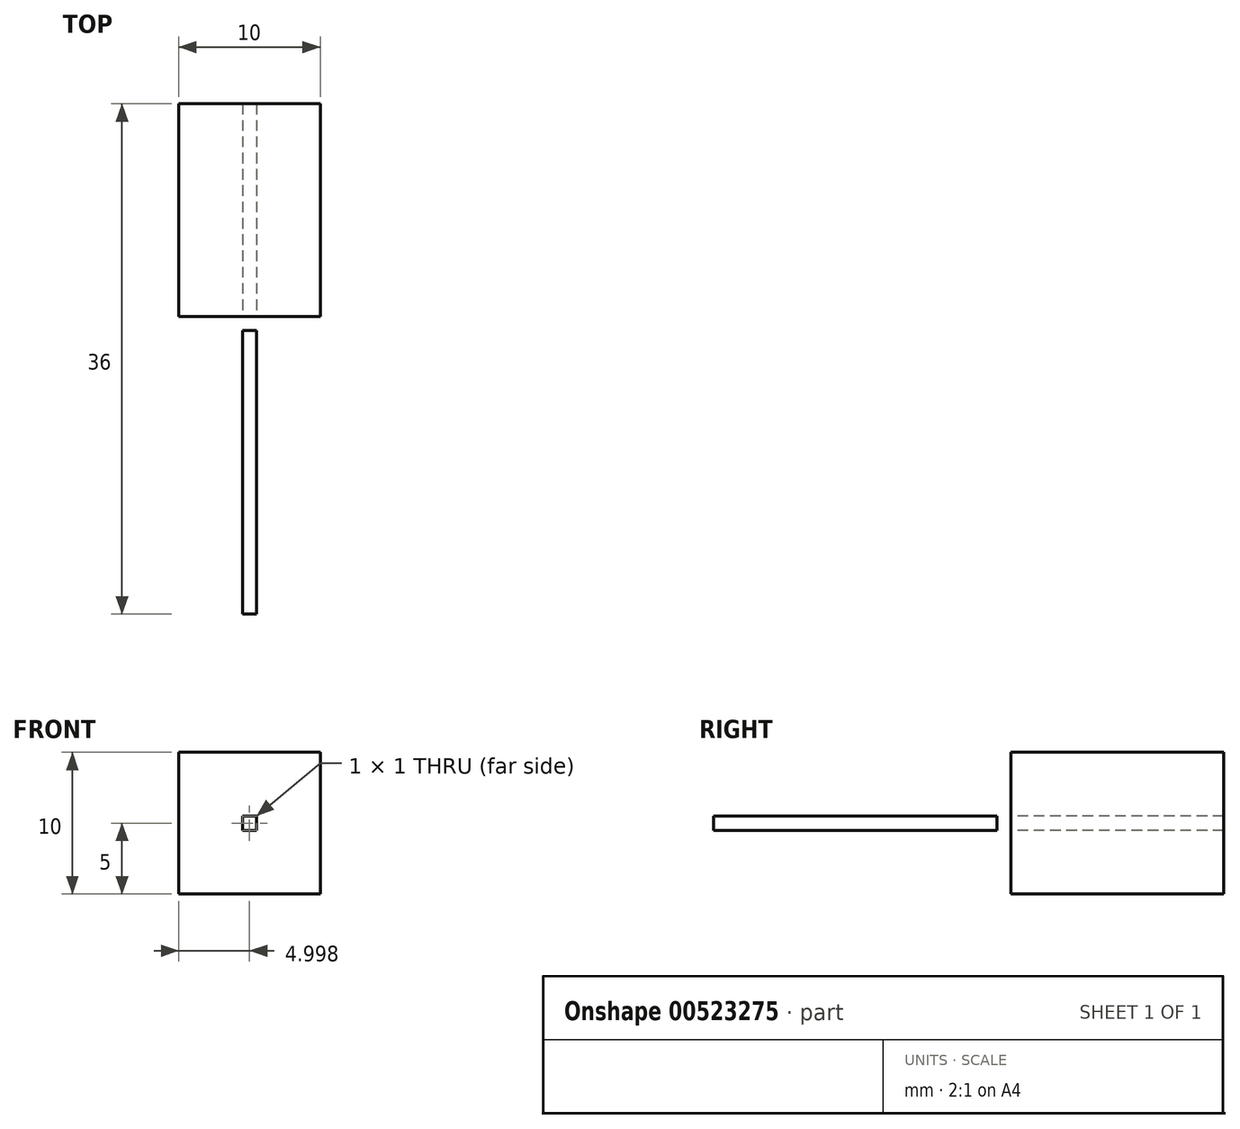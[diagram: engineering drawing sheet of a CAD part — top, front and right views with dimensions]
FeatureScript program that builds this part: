
annotation { "Feature Type Name" : "Feature", "Feature Type Description" : "" }
export const myFeature = defineFeature(function(context is Context, id is Id, definition is map)
    precondition{}
    {
        {
            var Q0;
            Q0=qCreatedBy(makeId("Top.planeOp"),FACE);
            var sketch = newSketch(context, id + "F0", { "sketchPlane" : qUnion([Q0])});
            skLineSegment(sketch, "E0.bottom", {"start": v(-40.2, 12.75) * mm, "end": v(-39.2, 12.75) * mm});
            skLineSegment(sketch, "E0.top", {"start": v(-40.2, -7.25) * mm, "end": v(-39.2, -7.25) * mm});
            skLineSegment(sketch, "E0.left", {"start": v(-40.2, 12.75) * mm, "end": v(-40.2, -7.25) * mm});
            skLineSegment(sketch, "E0.right", {"start": v(-39.2, 12.75) * mm, "end": v(-39.2, -7.25) * mm});
            skLineSegment(sketch, "E1.bottom", {"start": v(-44.7, 28.75) * mm, "end": v(-34.7, 28.75) * mm});
            skLineSegment(sketch, "E1.top", {"start": v(-44.7, 13.75) * mm, "end": v(-34.7, 13.75) * mm});
            skLineSegment(sketch, "E1.left", {"start": v(-44.7, 28.75) * mm, "end": v(-44.7, 13.75) * mm});
            skLineSegment(sketch, "E1.right", {"start": v(-34.7, 28.75) * mm, "end": v(-34.7, 13.75) * mm});
            skSolve(sketch);
        }
        {
            var Q0;
            Q0=makeQuery(id+"F0.imprint","IMPRINT",FACE,{"disambiguationData":[TD([[makeQuery(id+"F0.imprint","IMPRINT",EDGE,{"derivedFrom":sQuery(id+"F0.wireOp",EDGE,"E0.bottom")}),-1.0]])]});
            extrude(context, id + "F1", {"entities" : qUnion([Q0]), "depth" : 1 * mm, "offsetDistance" : 25 * mm});
        }
        {
            var Q0;
            Q0=makeQuery(id+"F0.imprint","IMPRINT",FACE,{"disambiguationData":[TD([[makeQuery(id+"F0.imprint","IMPRINT",EDGE,{"derivedFrom":sQuery(id+"F0.wireOp",EDGE,"E1.bottom")}),-1.0]])]});
            extrude(context, id + "F2", {"entities" : qUnion([Q0]), "depth" : 10 * mm, "offsetDistance" : 25 * mm});
        }
        {
            var Q0;
            Q0=makeQuery(id+"F2.opExtrude","SWEPT_FACE",FACE,{"disambiguationData":[OSD([sQuery(id+"F0.wireOp",EDGE,"E1.top")])]});
            var sketch = newSketch(context, id + "F3", { "sketchPlane" : qUnion([Q0])});
            skLineSegment(sketch, "E2.bottom", {"start": v(-40.2, 5.5) * mm, "end": v(-39.2, 5.5) * mm});
            skLineSegment(sketch, "E2.top", {"start": v(-40.2, 4.5) * mm, "end": v(-39.2, 4.5) * mm});
            skLineSegment(sketch, "E2.left", {"start": v(-40.2, 5.5) * mm, "end": v(-40.2, 4.5) * mm});
            skLineSegment(sketch, "E2.right", {"start": v(-39.2, 5.5) * mm, "end": v(-39.2, 4.5) * mm});
            skSolve(sketch);
        }
        {
            var Q0;
            Q0=makeQuery(id+"F3.imprint","IMPRINT",FACE,{"disambiguationData":[TD([[makeQuery(id+"F3.imprint","IMPRINT",EDGE,{"derivedFrom":sQuery(id+"F3.wireOp",EDGE,"E2.bottom")}),-1.0]])]});
            extrude(context, id + "F4", {"entities" : qUnion([Q0]), "operationType" : NewBodyOperationType.REMOVE, "oppositeDirection" : true, "depth" : 25 * mm, "offsetDistance" : 25 * mm});
        }
        {
            var Q0;
            Q0=makeQuery(id+"F1.opExtrude","SWEPT_BODY",BODY,{"disambiguationData":[OSD([sQuery(id+"F0.wireOp",EDGE,"E0.bottom"),sQuery(id+"F0.wireOp",EDGE,"E0.top"),sQuery(id+"F0.wireOp",EDGE,"E0.left"),sQuery(id+"F0.wireOp",EDGE,"E0.right")])]});
            transform(context, id + "F5", {"entities" : qUnion([Q0]), "transformType" : TransformType.TRANSLATION_3D, "dx" : 0 * mm, "dy" : 0 * mm, "dz" : 4.5 * mm, "makeCopy" : false});
        }
    });
